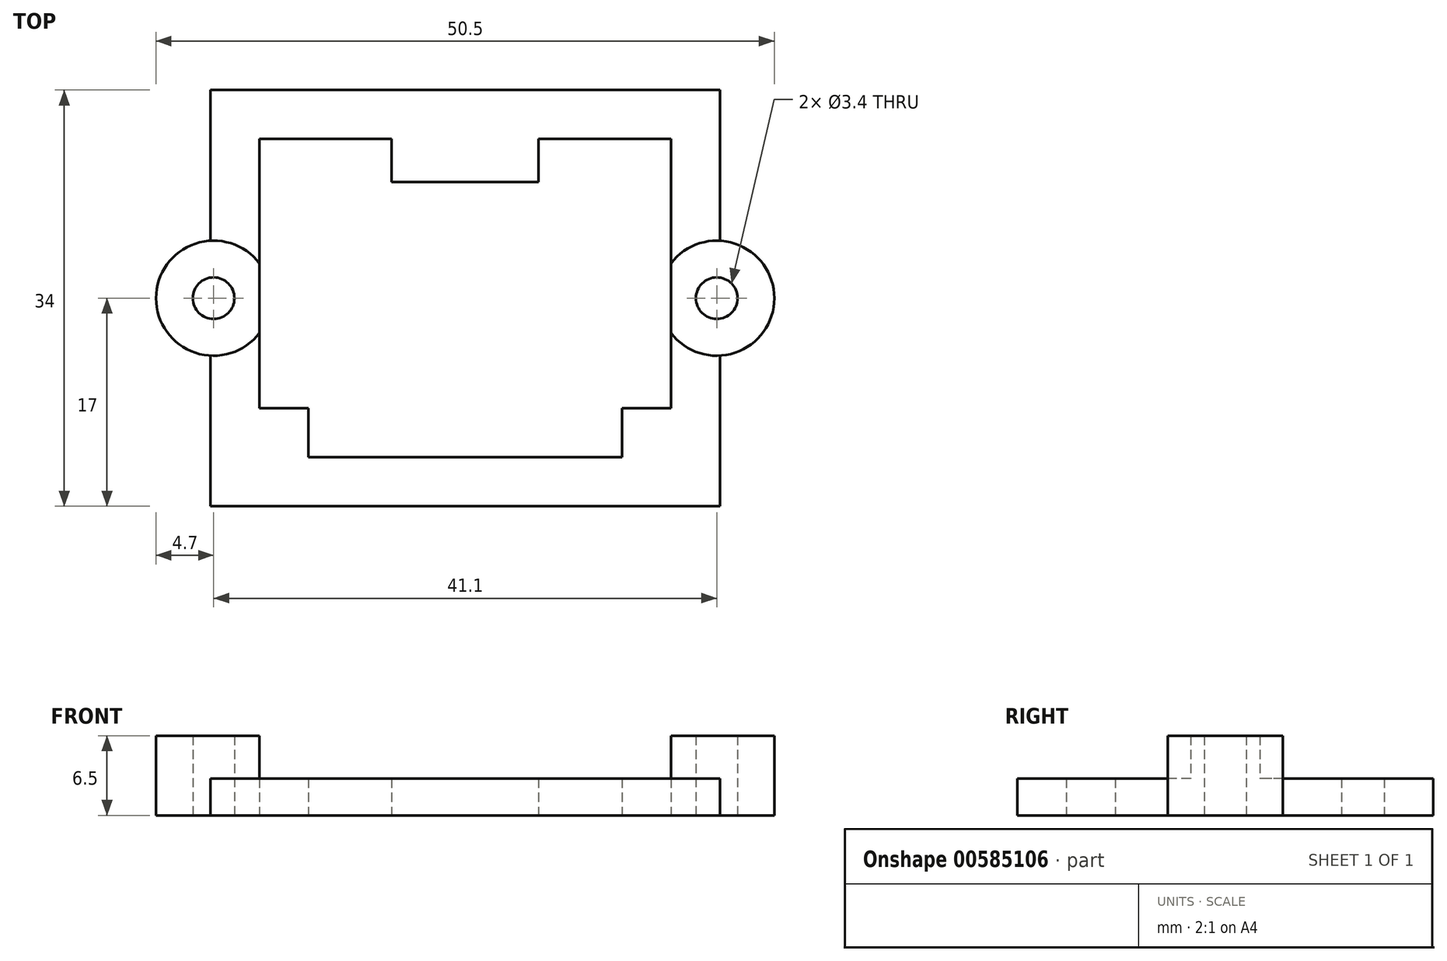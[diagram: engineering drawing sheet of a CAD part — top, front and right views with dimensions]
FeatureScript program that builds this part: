
annotation { "Feature Type Name" : "Feature", "Feature Type Description" : "" }
export const myFeature = defineFeature(function(context is Context, id is Id, definition is map)
    precondition{}
    {
        {
            var Q0;
            Q0=qCreatedBy(makeId("Top.planeOp"),FACE);
            var sketch = newSketch(context, id + "F0", { "sketchPlane" : qUnion([Q0])});
            skLineSegment(sketch, "E0.top", {"start": v(-6, 9.5) * mm, "end": v(6, 9.5) * mm});
            skPoint(sketch, "E0.middle", {"position": v(0, 0) * mm});
            skLineSegment(sketch, "E1.bottom", {"start": v(-20.8, -17) * mm, "end": v(20.8, -17) * mm});
            skLineSegment(sketch, "E1.top", {"start": v(-20.8, 17) * mm, "end": v(20.8, 17) * mm});
            skLineSegment(sketch, "E1.left", {"start": v(-20.8, -17) * mm, "end": v(-20.8, -4.7) * mm});
            skLineSegment(sketch, "E1.right", {"start": v(20.8, -17) * mm, "end": v(20.8, -4.7) * mm});
            skLineSegment(sketch, "E2", {"start": v(-12.8, -9) * mm, "end": v(-12.8, -13) * mm});
            skLineSegment(sketch, "E3", {"start": v(-12.8, -13) * mm, "end": v(12.8, -13) * mm});
            skLineSegment(sketch, "E4", {"start": v(12.8, -13) * mm, "end": v(12.8, -9) * mm});
            skLineSegment(sketch, "E5", {"start": v(-12.8, -9) * mm, "end": v(-16.8, -9) * mm});
            skLineSegment(sketch, "E6", {"start": v(-16.8, -9) * mm, "end": v(-16.8, 13) * mm});
            skLineSegment(sketch, "E7", {"start": v(-16.8, 13) * mm, "end": v(-6, 13) * mm});
            skLineSegment(sketch, "E8", {"start": v(6, 13) * mm, "end": v(16.8, 13) * mm});
            skLineSegment(sketch, "E9", {"start": v(16.8, 13) * mm, "end": v(16.8, -9) * mm});
            skLineSegment(sketch, "E10", {"start": v(16.8, -9) * mm, "end": v(12.8, -9) * mm});
            skLineSegment(sketch, "E11", {"start": v(6, 13) * mm, "end": v(6, 9.5) * mm});
            skLineSegment(sketch, "E12", {"start": v(-6, 13) * mm, "end": v(-6, 9.5) * mm});
            skPoint(sketch, "E13.orphan", {"position": v(-14, 9.5) * mm});
            skPoint(sketch, "E14.orphan", {"position": v(14, 9.5) * mm});
            skLineSegment(sketch, "E15", {"start": v(0, 0) * mm, "end": v(-16.8, 0) * mm, "construction": true});
            skLineSegment(sketch, "E16", {"start": v(0, 0) * mm, "end": v(16.8, 0) * mm, "construction": true});
            skLineSegment(sketch, "E17", {"start": v(0, -13) * mm, "end": v(0, 0) * mm, "construction": true});
            skLineSegment(sketch, "E18", {"start": v(11.62, 13) * mm, "end": v(11.62, 0) * mm, "construction": true});
            skArc(sketch, "E19", {"start": v(-20.8, 4.7) * mm, "mid": v(-25.25, 0) * mm, "end": v(-20.8, -4.7) * mm});
            skLineSegment(sketch, "E20.trimOffspring", {"start": v(-20.8, 4.7) * mm, "end": v(-20.8, 17) * mm});
            skCircle(sketch, "E21", {"center": v(-20.55, 0) * mm, "radius": 1.7 * mm});
            skCircle(sketch, "E22.MirrorC", {"center": v(20.55, 0) * mm, "radius": 1.7 * mm});
            skArc(sketch, "E23.MirrorCS", {"start": v(20.8, 4.7) * mm, "mid": v(25.25, 0) * mm, "end": v(20.8, -4.7) * mm});
            skLineSegment(sketch, "E24.MirrorCS", {"start": v(20.8, 4.7) * mm, "end": v(20.8, 4.7) * mm});
            skLineSegment(sketch, "E25.MirrorCS", {"start": v(20.8, -4.7) * mm, "end": v(20.8, -4.7) * mm});
            skLineSegment(sketch, "E26.trimOffspring", {"start": v(20.8, 4.7) * mm, "end": v(20.8, 17) * mm});
            skSolve(sketch);
        }
        {
            var Q0;
            Q0 = qSketchRegion(id + "F0", true);
            extrude(context, id + "F1", {"entities" : qUnion([Q0]), "depth" : 3 * mm, "offsetDistance" : 25 * mm});
        }
        {
            var Q0;
            Q0=makeQuery(id+"F1.opExtrude","CAP_FACE",FACE,{"disambiguationData":[OSD([sQuery(id+"F0.wireOp",EDGE,"E0.top"),sQuery(id+"F0.wireOp",EDGE,"E1.bottom"),sQuery(id+"F0.wireOp",EDGE,"E1.top"),sQuery(id+"F0.wireOp",EDGE,"E1.left"),sQuery(id+"F0.wireOp",EDGE,"E1.right"),sQuery(id+"F0.wireOp",EDGE,"E2"),sQuery(id+"F0.wireOp",EDGE,"E3"),sQuery(id+"F0.wireOp",EDGE,"E4"),sQuery(id+"F0.wireOp",EDGE,"E5"),sQuery(id+"F0.wireOp",EDGE,"E6"),sQuery(id+"F0.wireOp",EDGE,"E7"),sQuery(id+"F0.wireOp",EDGE,"E8"),sQuery(id+"F0.wireOp",EDGE,"E9"),sQuery(id+"F0.wireOp",EDGE,"E10"),sQuery(id+"F0.wireOp",EDGE,"E11"),sQuery(id+"F0.wireOp",EDGE,"E12"),sQuery(id+"F0.wireOp",EDGE,"E19"),sQuery(id+"F0.wireOp",EDGE,"E20.trimOffspring"),sQuery(id+"F0.wireOp",EDGE,"E21"),sQuery(id+"F0.wireOp",EDGE,"E22.MirrorC"),sQuery(id+"F0.wireOp",EDGE,"E23.MirrorCS"),sQuery(id+"F0.wireOp",EDGE,"E26.trimOffspring")])],"isStart":false});
            var sketch = newSketch(context, id + "F2", { "sketchPlane" : qUnion([Q0])});
            skArc(sketch, "E27", {"start": v(-16.8, 2.83) * mm, "mid": v(-25.25, 0) * mm, "end": v(-16.8, -2.83) * mm});
            skArc(sketch, "E28", {"start": v(16.8, 2.83) * mm, "mid": v(25.25, 0) * mm, "end": v(16.8, -2.83) * mm});
            skLineSegment(sketch, "E29", {"start": v(-16.8, -2.83) * mm, "end": v(-16.8, 2.83) * mm});
            skLineSegment(sketch, "E30", {"start": v(16.8, 2.83) * mm, "end": v(16.8, -2.83) * mm});
            skCircle(sketch, "E31.0", {"center": v(-20.55, 0) * mm, "radius": 1.7 * mm});
            skCircle(sketch, "E31.1", {"center": v(20.55, 0) * mm, "radius": 1.7 * mm});
            skSolve(sketch);
        }
        {
            var Q0;
            Q0 = qSketchRegion(id + "F2", true);
            extrude(context, id + "F3", {"entities" : qUnion([Q0]), "operationType" : NewBodyOperationType.ADD, "depth" : 3.5 * mm, "offsetDistance" : 25 * mm});
        }
    });
